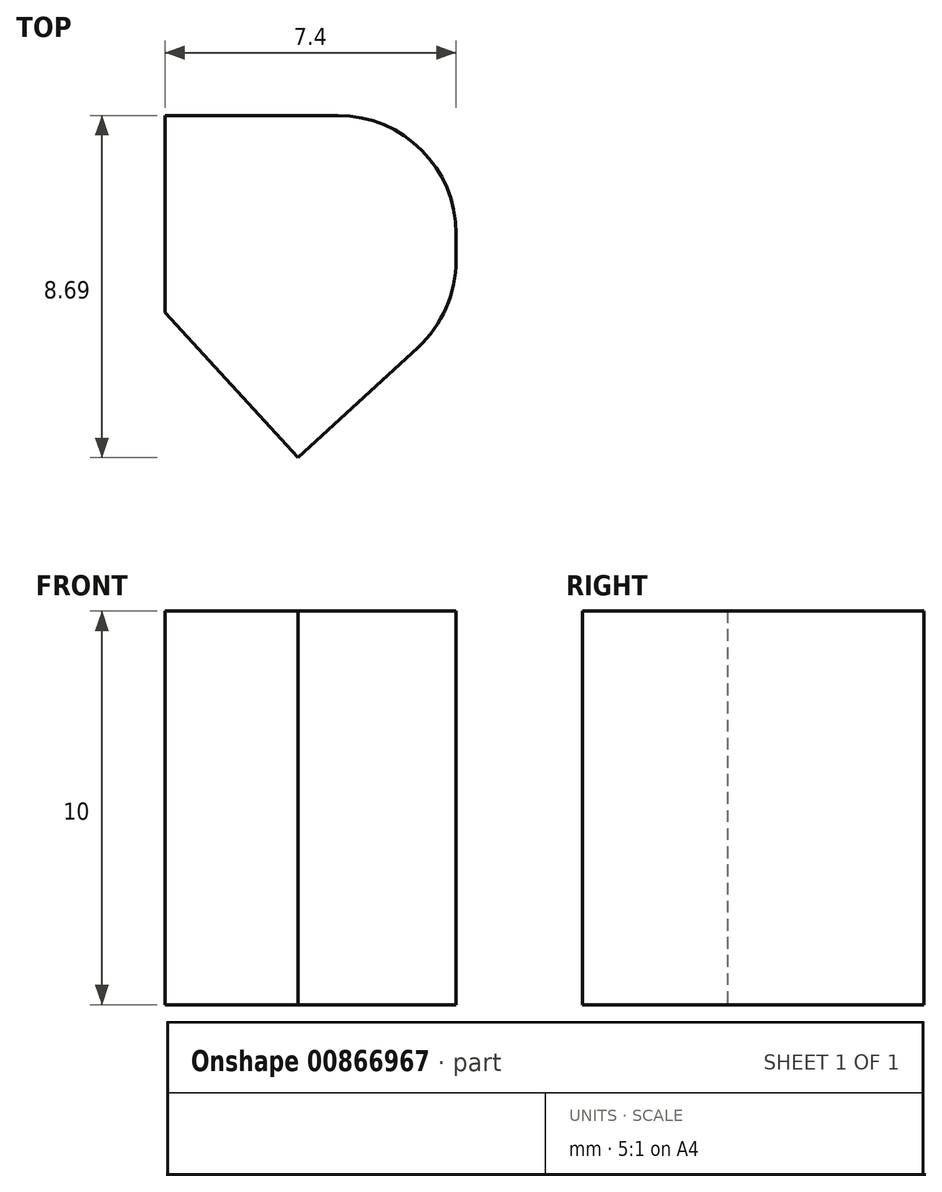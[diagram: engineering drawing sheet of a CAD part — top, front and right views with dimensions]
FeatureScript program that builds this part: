
annotation { "Feature Type Name" : "Feature", "Feature Type Description" : "" }
export const myFeature = defineFeature(function(context is Context, id is Id, definition is map)
    precondition{}
    {
        {
            var Q0;
            Q0=qCreatedBy(makeId("Top.planeOp"),FACE);
            var sketch = newSketch(context, id + "F0", { "sketchPlane" : qUnion([Q0])});
            skLineSegment(sketch, "E0", {"start": v(0, 0) * mm, "end": v(7.4, 0) * mm});
            skLineSegment(sketch, "E1", {"start": v(0, 0) * mm, "end": v(0, 5) * mm});
            skLineSegment(sketch, "E2", {"start": v(0, 5) * mm, "end": v(7.4, 5) * mm});
            skLineSegment(sketch, "E3", {"start": v(7.4, 5) * mm, "end": v(7.4, 0) * mm});
            skLineSegment(sketch, "E4", {"start": v(7.4, 0) * mm, "end": v(-1.74, -8.37) * mm});
            skLineSegment(sketch, "E5", {"start": v(-1.74, -8.37) * mm, "end": v(-9.14, -8.37) * mm});
            skLineSegment(sketch, "E6", {"start": v(0, 0) * mm, "end": v(-9.14, -8.37) * mm});
            skLineSegment(sketch, "E7", {"start": v(0, 0) * mm, "end": v(3.38, -3.69) * mm});
            skSolve(sketch);
        }
        {
            var Q0;
            Q0=makeQuery(id+"F0.imprint","IMPRINT",FACE,{"disambiguationData":[TD([[makeQuery(id+"F0.imprint","IMPRINT",EDGE,{"derivedFrom":sQuery(id+"F0.wireOp",EDGE,"E0")}),1.0]])]});
            var Q1;
            {var subQ0=sQuery(id+"F0.wireOp",EDGE,"E0");Q1=makeQuery(id+"F0.imprint","IMPRINT",FACE,{"disambiguationData":[TD([[makeQuery(id+"F0.imprint","IMPRINT",EDGE,{"derivedFrom":subQ0}),-1.0]])]});}
            extrude(context, id + "F1", {"entities" : qUnion([Q0, Q1]), "depth" : 10 * mm, "offsetDistance" : 25 * mm});
        }
        {
            var Q0;
            Q0=makeQuery(id+"F1.opExtrude","SWEPT_EDGE",EDGE,{"disambiguationData":[OSD([sQuery(id+"F0.wireOp",EDGE,"E2"),sQuery(id+"F0.wireOp",EDGE,"E3")])]});
            var Q1;
            Q1=makeQuery(id+"F1.opExtrude","SWEPT_EDGE",EDGE,{"disambiguationData":[OSD([sQuery(id+"F0.wireOp",EDGE,"E0"),sQuery(id+"F0.wireOp",EDGE,"E3")])]});
            fillet(context, id + "F2", {"entities" : qUnion([Q0, Q1]), "radius" : 3 * mm, "tangentPropagation" : true, "allowEdgeOverflow" : false});
        }
    });
